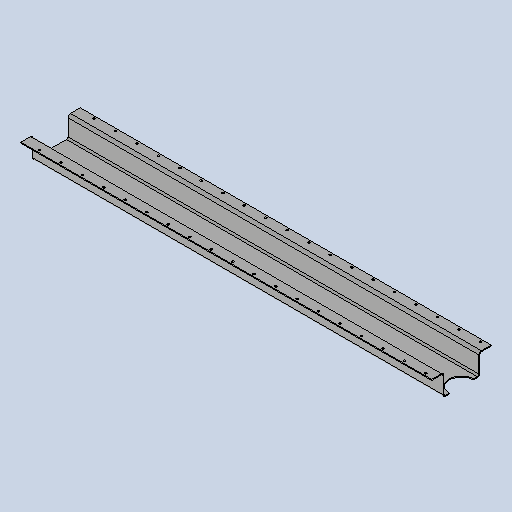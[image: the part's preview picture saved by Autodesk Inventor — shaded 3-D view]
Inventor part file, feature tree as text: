
AUTODESK INVENTOR PART (.ipt)
format: ipt  version: 2025 (Build 290162010, 162A)  size: 264,192 bytes
history: native  units: mm
features: sheet_metal_op x7, sketch x5, other x5, extrude x1, pattern_linear x1, mirror x1, projected_geometry x1
ambient origin geometry x8: Origin, YZ Plane, XZ Plane, XY Plane, X Axis, Y Axis, Z Axis, Center Point
bodies: Solid1 (feature_tree)
feature tree (21):
  sheet_metal_op  "Face1"
  sheet_metal_op  "Flange4"
  extrude  "Extrusion2"  Depth=3.0mm
  sheet_metal_op  "Flange5"
  pattern_linear  "Rectangular Pattern2"  Count1=12  [1 undecoded]
  mirror  "Mirror3"
  sketch  "Sketch1"  dims[d5=1340.0mm d6=3.0mm d30=120.0mm]
  other  "Plate1"
  sketch  "Sketch6"  dims[d60=3.0mm]
  other  "Plate5"
  sheet_metal_op  "Bend4"
  sheet_metal_op  "Corner4"
  sketch  "Sketch7"  dims[d61=1.5mm]
  sketch  "Sketch9"  dims[d62=6.0mm]
  other  "Plate6"
  sheet_metal_op  "Bend5"
  sheet_metal_op  "Corner5"
  sketch  "Sketch10"  dims[d63=5.0mm d64=70.0mm d65=90.0deg d66=5.0mm d67=12.0mm d68=3.0mm d69=5.0mm d70=80.0mm d71=0.0mm d72=0.0mm d81=3.0mm d82=1.5mm d83=6.0mm d84=5.0mm d85=40.0mm d86=90.0deg d87=5.0mm d88=12.0mm d89=3.0mm d90=5.0mm d91=7.0mm d92=27.0mm d93=3.0mm d94=0.0mm d95=300.0mm d97=70.0mm d98=8.0mm d99=10.0mm]
  projected_geometry  "Projected Loop3"
  other  "Cut1"
  other  "Definition1"
note: 1 required parameter value undecoded (feature->parameter linkage not recoverable at this tier; creation-order binding heuristic only, values carry confidence <= 0.55)
